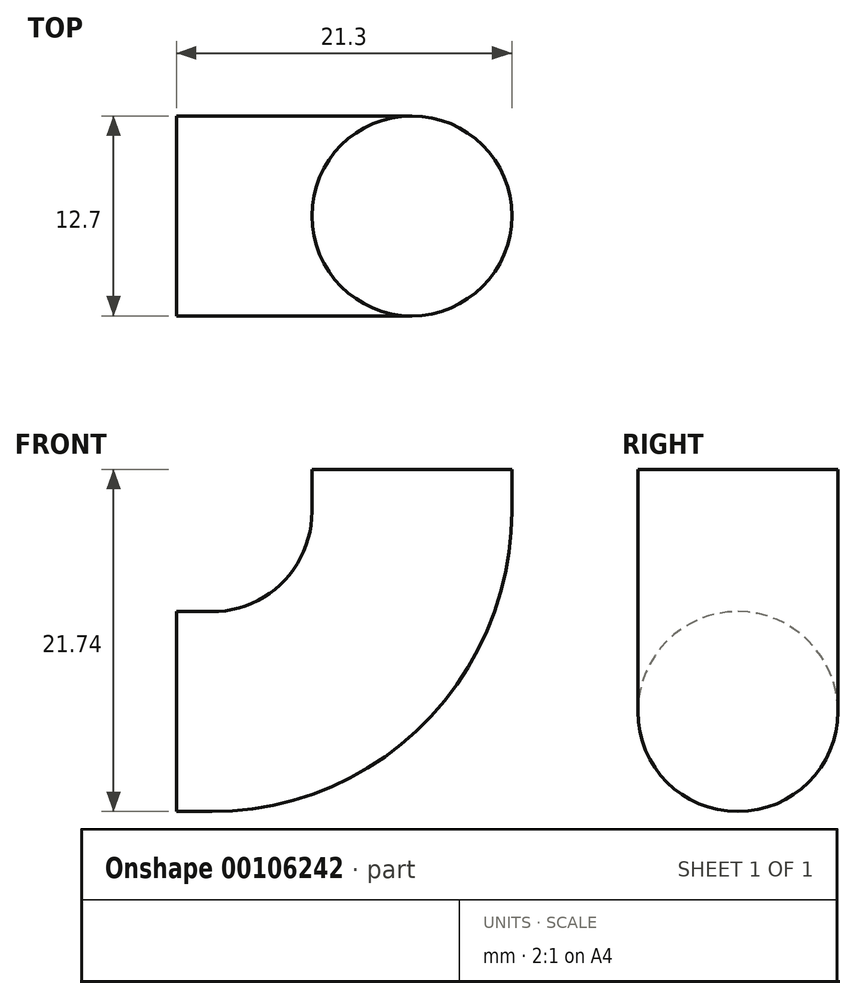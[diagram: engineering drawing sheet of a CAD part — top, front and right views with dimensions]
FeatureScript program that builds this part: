
annotation { "Feature Type Name" : "Feature", "Feature Type Description" : "" }
export const myFeature = defineFeature(function(context is Context, id is Id, definition is map)
    precondition{}
    {
        {
            var Q0;
            Q0=qCreatedBy(makeId("Front.planeOp"),FACE);
            var sketch = newSketch(context, id + "F0", { "sketchPlane" : qUnion([Q0])});
            skLineSegment(sketch, "E0", {"start": v(0, 15.4) * mm, "end": v(0, 12.7) * mm});
            skLineSegment(sketch, "E1", {"start": v(-12.7, 0) * mm, "end": v(-14.95, 0) * mm});
            skPoint(sketch, "E2.visualSharp", {"position": v(0, 0) * mm});
            skArc(sketch, "E2.filletArc", {"start": v(-12.7, 0) * mm, "mid": v(-3.72, 3.72) * mm, "end": v(0, 12.7) * mm});
            skSolve(sketch);
        }
        {
            var Q0;
            Q0=sQuery(id+"F0.wireOp",VERTEX,"E0.start");
            var Q1;
            Q1=qCreatedBy(makeId("Top.planeOp"),FACE);
            cPlane(context, id + "F1", {"entities" : qUnion([Q0, Q1]), "cplaneType" : CPlaneType.PLANE_POINT, "offset" : 25.4 * mm, "width" : 152.4 * mm, "height" : 152.4 * mm});
        }
        {
            var Q0;
            Q0=qCreatedBy(id+"F1.planeOp",FACE);
            var sketch = newSketch(context, id + "F2", { "sketchPlane" : qUnion([Q0])});
            skCircle(sketch, "E3", {"center": v(0, 0) * mm, "radius": 6.35 * mm});
            skSolve(sketch);
        }
        {
            var Q0;
            Q0=makeQuery(id+"F2.imprint","IMPRINT",FACE,{"disambiguationData":[TD([[makeQuery(id+"F2.imprint","IMPRINT",EDGE,{"derivedFrom":sQuery(id+"F2.wireOp",EDGE,"E3")}),1.0]])]});
            var Q1;
            Q1=sQuery(id+"F0.wireOp",EDGE,"E2.filletArc");
            var Q2;
            Q2=sQuery(id+"F0.wireOp",EDGE,"E0");
            var Q3;
            Q3=sQuery(id+"F0.wireOp",EDGE,"E1");
            sweep(context, id + "F3", {"profiles" : qUnion([Q0]), "path" : qUnion([Q1, Q2, Q3])});
        }
    });
